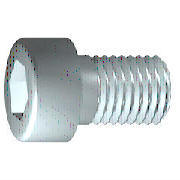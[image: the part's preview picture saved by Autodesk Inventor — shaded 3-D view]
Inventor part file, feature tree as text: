
AUTODESK INVENTOR PART (.ipt)
format: ipt  version: 2019.1 (Build 231200000, 200)  size: 190,976 bytes
history: native  units: mm (DEFAULTED — no unit token found)
features: sketch x2, extrude x1, plane x1, fillet x1
ambient origin geometry x7: Origin, YZ Plane, XY Plane, X Axis, Y Axis, Z Axis, Center Point
bodies: Solid1 (feature_tree), Body (feature_tree)
feature tree (5):
  extrude  "Slot"  Depth=3.5052mm
  plane  "Work Plane1"
  fillet  "Fillet2"  Radius=3.5052mm
  sketch  "Sketch1"  dims[d1=10.715552mm d2=1.984348mm d3=3.5052mm]
  sketch  "Sketch2"  dims[d4=1.6256mm d5=60.0deg d6=3.5052mm d7=3.5052mm d8=3.196904mm d9=5.7404mm d10=90.0deg d11=10.0mm d12=0.0mm d13=10.715552mm d14=0.0mm d15=0.47244mm d16=0.47244mm d17=0.3302mm d19=0.0mm d26=12.7mm d27=45.0deg d28=0.0mm d29=0.0mm d30=0.127mm]
